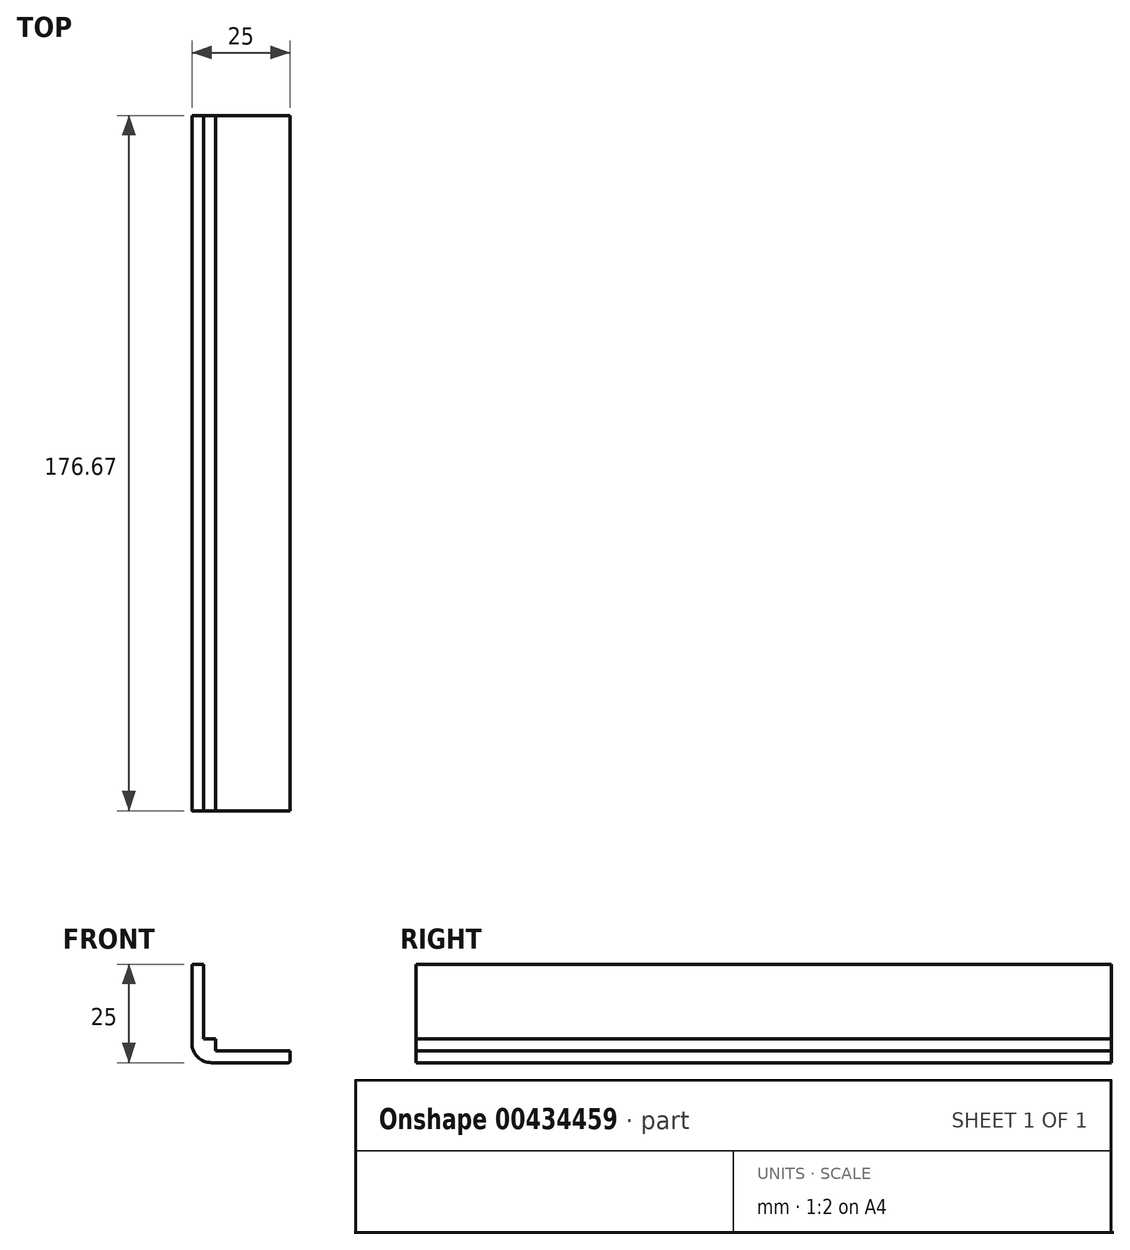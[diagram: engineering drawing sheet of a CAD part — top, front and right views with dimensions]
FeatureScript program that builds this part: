
annotation { "Feature Type Name" : "Feature", "Feature Type Description" : "" }
export const myFeature = defineFeature(function(context is Context, id is Id, definition is map)
    precondition{}
    {
        {
            var Q0;
            Q0=qCreatedBy(makeId("Front.planeOp"),FACE);
            var sketch = newSketch(context, id + "F0", { "sketchPlane" : qUnion([Q0])});
            skLineSegment(sketch, "E0", {"start": v(0, 25) * mm, "end": v(0, 0) * mm});
            skLineSegment(sketch, "E1", {"start": v(0, 0) * mm, "end": v(25, 0) * mm});
            skLineSegment(sketch, "E2", {"start": v(25, 0) * mm, "end": v(25, 3) * mm});
            skLineSegment(sketch, "E3", {"start": v(25, 3) * mm, "end": v(6, 3) * mm});
            skLineSegment(sketch, "E4", {"start": v(6, 3) * mm, "end": v(6, 6) * mm});
            skLineSegment(sketch, "E5", {"start": v(6, 6) * mm, "end": v(3, 6) * mm});
            skLineSegment(sketch, "E6", {"start": v(3, 6) * mm, "end": v(3, 25) * mm});
            skLineSegment(sketch, "E7", {"start": v(3, 25) * mm, "end": v(0, 25) * mm});
            skSolve(sketch);
        }
        {
            var Q0;
            Q0=makeQuery(id+"F0.imprint","IMPRINT",FACE,{"disambiguationData":[TD([[makeQuery(id+"F0.imprint","IMPRINT",EDGE,{"derivedFrom":sQuery(id+"F0.wireOp",EDGE,"E0")}),1.0]])]});
            extrude(context, id + "F1", {"entities" : qUnion([Q0]), "depth" : 176.67 * mm});
        }
        {
            var Q0;
            Q0=makeQuery(id+"F1.opExtrude","SWEPT_EDGE",EDGE,{"disambiguationData":[OSD([sQuery(id+"F0.wireOp",EDGE,"E0"),sQuery(id+"F0.wireOp",EDGE,"E1")])]});
            fillet(context, id + "F2", {"entities" : qUnion([Q0]), "radius" : 5 * mm, "tangentPropagation" : true, "allowEdgeOverflow" : false});
        }
        {
            var Q0;
            Q0=makeQuery(id+"F1.opExtrude","SWEPT_EDGE",EDGE,{"disambiguationData":[OSD([sQuery(id+"F0.wireOp",EDGE,"E0"),sQuery(id+"F0.wireOp",EDGE,"E7")])]});
            var Q1;
            Q1=makeQuery(id+"F1.opExtrude","SWEPT_EDGE",EDGE,{"disambiguationData":[OSD([sQuery(id+"F0.wireOp",EDGE,"E1"),sQuery(id+"F0.wireOp",EDGE,"E2")])]});
            fillet(context, id + "F3", {"entities" : qUnion([Q0, Q1]), "radius" : .5 * mm, "tangentPropagation" : true, "allowEdgeOverflow" : false});
        }
    });
